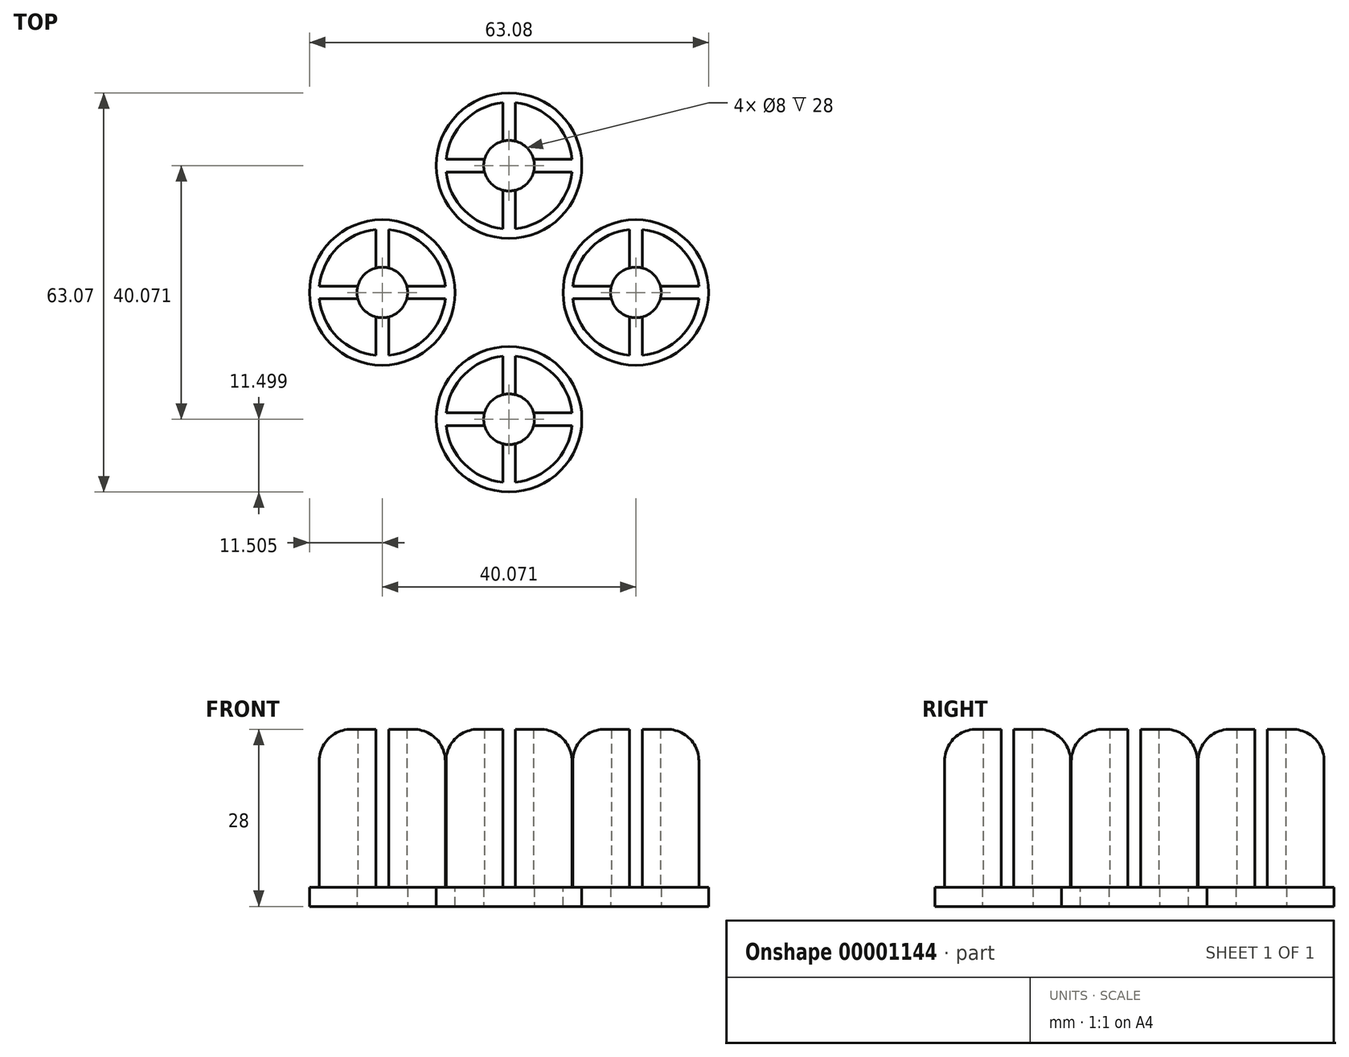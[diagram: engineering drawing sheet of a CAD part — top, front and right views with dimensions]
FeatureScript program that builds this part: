
annotation { "Feature Type Name" : "Feature", "Feature Type Description" : "" }
export const myFeature = defineFeature(function(context is Context, id is Id, definition is map)
    precondition{}
    {
        {
            var Q0;
            Q0=qCreatedBy(makeId("Top.planeOp"),FACE);
            var sketch = newSketch(context, id + "F0", { "sketchPlane" : qUnion([Q0])});
            skCircle(sketch, "E0", {"center": v(0, 0) * mm, "radius": 10 * mm});
            skCircle(sketch, "E1", {"center": v(0, 0) * mm, "radius": 4 * mm});
            skSolve(sketch);
        }
        {
            var Q0;
            Q0 = qSketchRegion(id + "F0", true);
            extrude(context, id + "F1", {"entities" : qUnion([Q0]), "depth" : 25 * mm});
        }
        {
            var Q0;
            Q0=qCreatedBy(makeId("Top.planeOp"),FACE);
            var sketch = newSketch(context, id + "F2", { "sketchPlane" : qUnion([Q0])});
            skCircle(sketch, "E2", {"center": v(0, 0) * mm, "radius": 11.5 * mm});
            skCircle(sketch, "E3", {"center": v(0, 0) * mm, "radius": 4 * mm});
            skSolve(sketch);
        }
        {
            var Q0;
            Q0 = qSketchRegion(id + "F2", true);
            extrude(context, id + "F3", {"entities" : qUnion([Q0]), "operationType" : NewBodyOperationType.ADD, "oppositeDirection" : true, "depth" : 3 * mm});
        }
        {
            var Q0;
            Q0=qCreatedBy(makeId("Top.planeOp"),FACE);
            var sketch = newSketch(context, id + "F4", { "sketchPlane" : qUnion([Q0])});
            skLineSegment(sketch, "E4.top", {"start": v(-16.4, 1) * mm, "end": v(17.64, 1) * mm});
            skLineSegment(sketch, "E5.top", {"start": v(-16.4, -1) * mm, "end": v(18.02, -1) * mm});
            skLineSegment(sketch, "E6.right", {"start": v(-1, 15.85) * mm, "end": v(-1, -19.36) * mm});
            skLineSegment(sketch, "E7.right", {"start": v(1, 15.85) * mm, "end": v(1, -19.36) * mm});
            skLineSegment(sketch, "E8", {"start": v(-1, 15.85) * mm, "end": v(1, 15.85) * mm});
            skLineSegment(sketch, "E9", {"start": v(-16.4, 1) * mm, "end": v(-16.4, -1) * mm});
            skLineSegment(sketch, "E10", {"start": v(17.64, 1) * mm, "end": v(18.02, -1) * mm});
            skLineSegment(sketch, "E11", {"start": v(-1, -19.36) * mm, "end": v(1, -19.36) * mm});
            skSolve(sketch);
        }
        {
            var Q0;
            Q0 = qSketchRegion(id + "F4", true);
            extrude(context, id + "F5", {"entities" : qUnion([Q0]), "operationType" : NewBodyOperationType.REMOVE, "depth" : 25 * mm});
        }
        {
            var Q0;
            {var subQ0=sQuery(id+"F0.wireOp",EDGE,"E0");var subQ2=sQuery(id+"F4.wireOp",EDGE,"E5.top");Q0=makeQuery(id+"F5.boolean.opBoolean","SPLIT",EDGE,{"disambiguationData":[TD([makeQuery(id+"F5.opExtrude","SWEPT_FACE",FACE,{"disambiguationData":[OSD([subQ2]),TDD([makeQuery(id+"F4.imprint","IMPRINT",EDGE,{"disambiguationData":[TD([[makeQuery(id+"F4.imprint","INTERSECT",VERTEX,{"derivedFrom":[subQ2,sQuery(id+"F4.wireOp",EDGE,"E10")]}),1.0]])],"derivedFrom":subQ2})])]})])],"derivedFrom":makeQuery(id+"F1.opExtrude","CAP_EDGE",EDGE,{"disambiguationData":[OSD([subQ0])],"isStart":false})});}
            var Q1;
            {var subQ0=sQuery(id+"F0.wireOp",EDGE,"E0");var subQ2=sQuery(id+"F4.wireOp",EDGE,"E4.top");Q1=makeQuery(id+"F5.boolean.opBoolean","SPLIT",EDGE,{"disambiguationData":[TD([makeQuery(id+"F5.opExtrude","SWEPT_FACE",FACE,{"disambiguationData":[OSD([subQ2]),TDD([makeQuery(id+"F4.imprint","IMPRINT",EDGE,{"disambiguationData":[TD([[makeQuery(id+"F4.imprint","INTERSECT",VERTEX,{"derivedFrom":[subQ2,sQuery(id+"F4.wireOp",EDGE,"E10")]}),1.0]])],"derivedFrom":subQ2})])]})])],"derivedFrom":makeQuery(id+"F1.opExtrude","CAP_EDGE",EDGE,{"disambiguationData":[OSD([subQ0])],"isStart":false})});}
            var Q2;
            {var subQ0=sQuery(id+"F0.wireOp",EDGE,"E0");var subQ2=sQuery(id+"F4.wireOp",EDGE,"E4.top");Q2=makeQuery(id+"F5.boolean.opBoolean","SPLIT",EDGE,{"disambiguationData":[TD([makeQuery(id+"F5.opExtrude","SWEPT_FACE",FACE,{"disambiguationData":[OSD([subQ2]),TDD([makeQuery(id+"F4.imprint","IMPRINT",EDGE,{"disambiguationData":[TD([[makeQuery(id+"F4.imprint","INTERSECT",VERTEX,{"derivedFrom":[subQ2,sQuery(id+"F4.wireOp",EDGE,"E9")]}),-1.0]])],"derivedFrom":subQ2})])]})])],"derivedFrom":makeQuery(id+"F1.opExtrude","CAP_EDGE",EDGE,{"disambiguationData":[OSD([subQ0])],"isStart":false})});}
            var Q3;
            {var subQ0=sQuery(id+"F0.wireOp",EDGE,"E0");var subQ2=sQuery(id+"F4.wireOp",EDGE,"E5.top");Q3=makeQuery(id+"F5.boolean.opBoolean","SPLIT",EDGE,{"disambiguationData":[TD([makeQuery(id+"F5.opExtrude","SWEPT_FACE",FACE,{"disambiguationData":[OSD([subQ2]),TDD([makeQuery(id+"F4.imprint","IMPRINT",EDGE,{"disambiguationData":[TD([[makeQuery(id+"F4.imprint","INTERSECT",VERTEX,{"derivedFrom":[subQ2,sQuery(id+"F4.wireOp",EDGE,"E9")]}),-1.0]])],"derivedFrom":subQ2})])]})])],"derivedFrom":makeQuery(id+"F1.opExtrude","CAP_EDGE",EDGE,{"disambiguationData":[OSD([subQ0])],"isStart":false})});}
            fillet(context, id + "F6", {"entities" : qUnion([Q0, Q1, Q2, Q3]), "radius" : 5 * mm, "tangentPropagation" : true, "allowEdgeOverflow" : false});
        }
        {
            var Q0;
            Q0=qCreatedBy(makeId("Top.planeOp"),FACE);
            var sketch = newSketch(context, id + "F7", { "sketchPlane" : qUnion([Q0])});
            skLineSegment(sketch, "E12.bottom", {"start": v(-110.46, -34.24) * mm, "end": v(-55.47, -34.24) * mm});
            skLineSegment(sketch, "E12.top", {"start": v(-110.46, -79.48) * mm, "end": v(-55.47, -79.48) * mm});
            skLineSegment(sketch, "E12.left", {"start": v(-110.46, -34.24) * mm, "end": v(-110.46, -79.48) * mm});
            skLineSegment(sketch, "E12.right", {"start": v(-55.47, -34.24) * mm, "end": v(-55.47, -79.48) * mm});
            skSolve(sketch);
        }
        {
            var Q0;
            Q0 = qSketchRegion(id + "F7", true);
            extrude(context, id + "F8", {"entities" : qUnion([Q0]), "depth" : 25 * mm});
        }
        {
            var Q0;
            Q0=makeQuery(id+"F8.opExtrude","SWEPT_BODY",BODY,{"disambiguationData":[OSD([sQuery(id+"F7.wireOp",EDGE,"E12.bottom"),sQuery(id+"F7.wireOp",EDGE,"E12.top"),sQuery(id+"F7.wireOp",EDGE,"E12.left"),sQuery(id+"F7.wireOp",EDGE,"E12.right")])]});
            deleteBodies(context, id + "F9", {"entities" : qUnion([Q0])});
        }
        {
            var Q0;
            Q0=qCreatedBy(makeId("Right.planeOp"),FACE);
            var sketch = newSketch(context, id + "F10", { "sketchPlane" : qUnion([Q0])});
            skLineSegment(sketch, "E13", {"start": v(-20.04, 51.85) * mm, "end": v(-20.04, -35.71) * mm, "construction": true});
            skSolve(sketch);
        }
        {
            var Q0;
            {var subQ0=sQuery(id+"F0.wireOp",EDGE,"E0");var subQ2=sQuery(id+"F4.wireOp",EDGE,"E4.top");var subQ5=sQuery(id+"F4.wireOp",EDGE,"E10");Q0=makeQuery(id+"F5.boolean.opBoolean","SPLIT",FACE,{"disambiguationData":[TD([makeQuery(id+"F5.opExtrude","SWEPT_FACE",FACE,{"disambiguationData":[OSD([subQ2]),TDD([makeQuery(id+"F4.imprint","IMPRINT",EDGE,{"disambiguationData":[TD([[makeQuery(id+"F4.imprint","INTERSECT",VERTEX,{"derivedFrom":[subQ2,subQ5]}),1.0]])],"derivedFrom":subQ2})])]})])],"derivedFrom":makeQuery(id+"F1.opExtrude","SWEPT_FACE",FACE,{"disambiguationData":[OSD([subQ0])]})});}
            var Q1;
            Q1=makeQuery(id+"F1.opExtrude","SWEPT_BODY",BODY,{"disambiguationData":[OSD([sQuery(id+"F0.wireOp",EDGE,"E0"),sQuery(id+"F0.wireOp",EDGE,"E1")])]});
            var Q2;
            Q2=sQuery(id+"F10.wireOp",EDGE,"E13");
            circularPattern(context, id + "F11", {"entities" : qUnion([Q1]), "axis" : qUnion([Q2]), "angle" : 90 * degree, "instanceCount" : 4});
        }
    });
